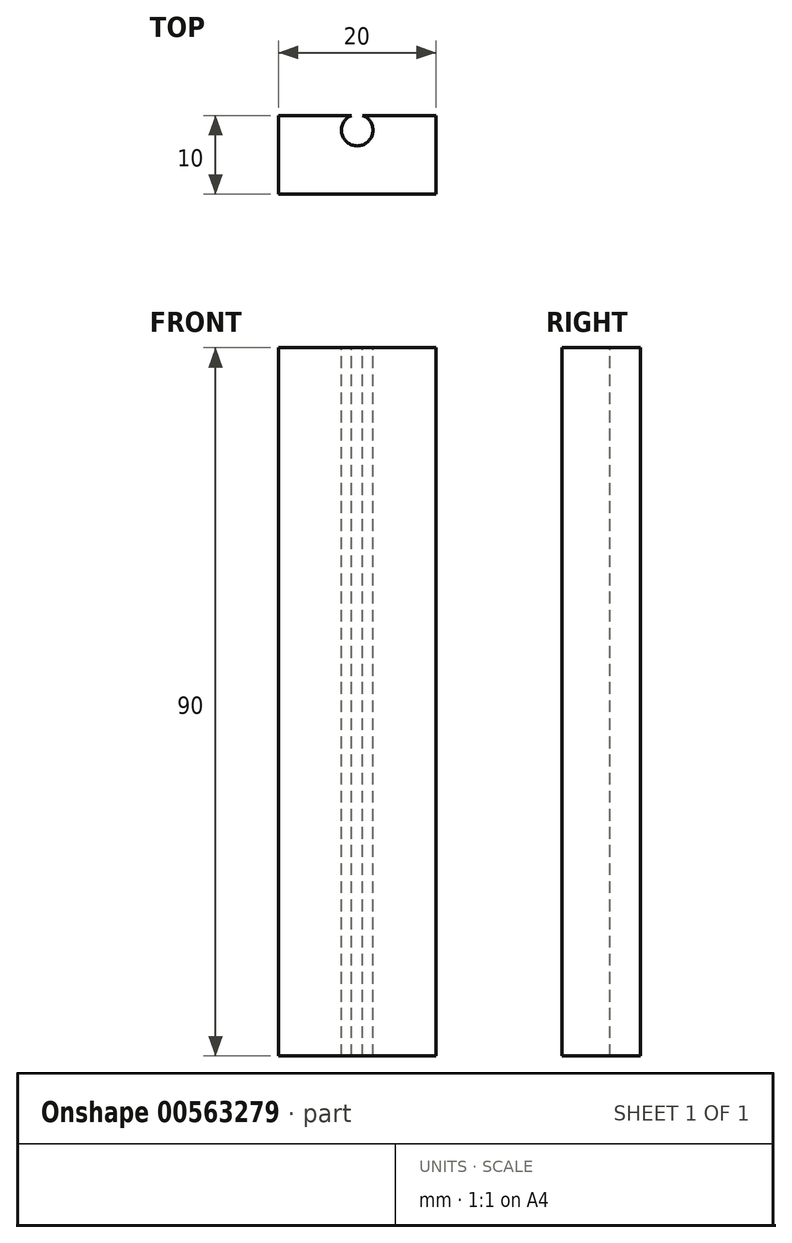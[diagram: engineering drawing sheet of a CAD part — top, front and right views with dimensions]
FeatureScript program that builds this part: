
annotation { "Feature Type Name" : "Feature", "Feature Type Description" : "" }
export const myFeature = defineFeature(function(context is Context, id is Id, definition is map)
    precondition{}
    {
        {
            var Q0;
            Q0=qCreatedBy(makeId("Top.planeOp"),FACE);
            var sketch = newSketch(context, id + "F0", { "sketchPlane" : qUnion([Q0])});
            skLineSegment(sketch, "E0.bottom", {"start": v(10, 10) * mm, "end": v(-10, 10) * mm});
            skLineSegment(sketch, "E0.left", {"start": v(10, 10) * mm, "end": v(10, 0) * mm});
            skLineSegment(sketch, "E0.right", {"start": v(-10, 10) * mm, "end": v(-10, 0) * mm});
            skPoint(sketch, "E0.middle", {"position": v(0, 0) * mm});
            skLineSegment(sketch, "E1", {"start": v(-10, 0) * mm, "end": v(10, 0) * mm});
            skPoint(sketch, "E0.top.end.orphan", {"position": v(-10, -10) * mm});
            skPoint(sketch, "E2.orphan", {"position": v(10, -10) * mm});
            skSolve(sketch);
        }
        {
            var Q0;
            Q0 = qSketchRegion(id + "F0", true);
            extrude(context, id + "F1", {"entities" : qUnion([Q0]), "oppositeDirection" : true, "depth" : 90 * mm, "offsetDistance" : 25 * mm});
        }
        {
            var Q0;
            Q0=makeQuery(id+"F0.imprint","IMPRINT",FACE,{"disambiguationData":[TD([[makeQuery(id+"F0.imprint","IMPRINT",EDGE,{"derivedFrom":sQuery(id+"F0.wireOp",EDGE,"E0.bottom")}),1.0]])]});
            var sketch = newSketch(context, id + "F2", { "sketchPlane" : qUnion([Q0])});
            skLineSegment(sketch, "E3", {"start": v(0, 9.13) * mm, "end": v(0, 8.13) * mm});
            skCircle(sketch, "E4", {"center": v(0, 8.13) * mm, "radius": 2 * mm});
            skSolve(sketch);
        }
        {
            var Q0;
            Q0 = qSketchRegion(id + "F2", true);
            var Q1;
            Q1=sQuery(id+"F2.wireOp",EDGE,"E4");
            extrude(context, id + "F3", {"entities" : qUnion([Q0]), "operationType" : NewBodyOperationType.REMOVE, "surfaceEntities" : qUnion([Q1]), "oppositeDirection" : true, "depth" : 150 * mm, "offsetDistance" : 25 * mm});
        }
    });
